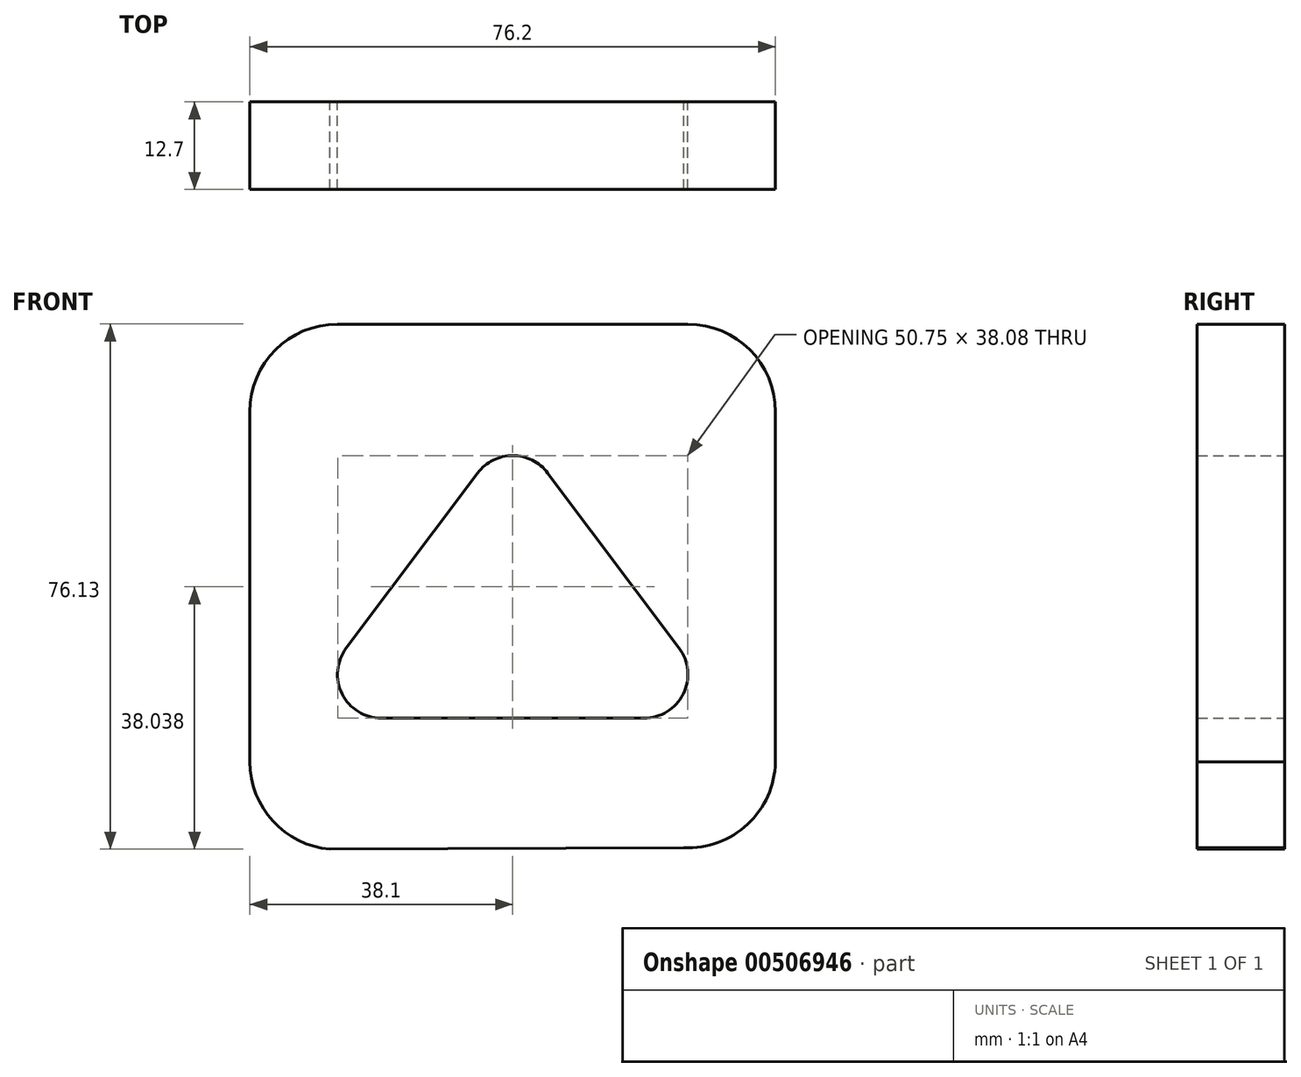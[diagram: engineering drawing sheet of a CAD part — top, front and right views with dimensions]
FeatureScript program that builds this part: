
annotation { "Feature Type Name" : "Feature", "Feature Type Description" : "" }
export const myFeature = defineFeature(function(context is Context, id is Id, definition is map)
    precondition{}
    {
        {
            var Q0;
            Q0=qCreatedBy(makeId("Front.planeOp"),FACE);
            var sketch = newSketch(context, id + "F0", { "sketchPlane" : qUnion([Q0])});
            skLineSegment(sketch, "E0", {"start": v(76.2, 12.68) * mm, "end": v(76.2, 63.48) * mm});
            skLineSegment(sketch, "E1", {"start": v(63.5, 76.18) * mm, "end": v(12.7, 76.18) * mm});
            skLineSegment(sketch, "E2", {"start": v(0, 63.48) * mm, "end": v(0, 12.7) * mm});
            skArc(sketch, "E3", {"start": v(13.97, 29.21) * mm, "mid": v(13.37, 22.56) * mm, "end": v(19.05, 19.05) * mm});
            skArc(sketch, "E4", {"start": v(57.15, 19.05) * mm, "mid": v(62.83, 22.56) * mm, "end": v(62.23, 29.21) * mm});
            skArc(sketch, "E5", {"start": v(43.18, 54.59) * mm, "mid": v(38.1, 57.13) * mm, "end": v(33.02, 54.59) * mm});
            skLineSegment(sketch, "E6", {"start": v(13.97, 29.21) * mm, "end": v(33.02, 54.59) * mm});
            skLineSegment(sketch, "E7", {"start": v(43.18, 54.59) * mm, "end": v(62.23, 29.21) * mm});
            skLineSegment(sketch, "E8", {"start": v(19.05, 19.05) * mm, "end": v(57.15, 19.05) * mm});
            skArc(sketch, "E9", {"start": v(12.7, 76.18) * mm, "mid": v(3.72, 72.46) * mm, "end": v(0, 63.48) * mm});
            skPoint(sketch, "E10.orphan", {"position": v(0, 76.18) * mm});
            skLineSegment(sketch, "E11", {"start": v(11.6, 0.05) * mm, "end": v(62.92, 0.26) * mm});
            skArc(sketch, "E12", {"start": v(0, 12.7) * mm, "mid": v(4.16, 3.3) * mm, "end": v(13.91, 0.06) * mm});
            skArc(sketch, "E13", {"start": v(76.2, 63.48) * mm, "mid": v(72.48, 72.46) * mm, "end": v(63.5, 76.18) * mm});
            skArc(sketch, "E14.trimOffspring", {"start": v(62.92, 0.26) * mm, "mid": v(72.18, 3.67) * mm, "end": v(76.2, 12.68) * mm});
            skSolve(sketch);
        }
        {
            var Q0;
            Q0=makeQuery(id+"F0.imprint","IMPRINT",FACE,{"disambiguationData":[TD([[makeQuery(id+"F0.imprint","IMPRINT",EDGE,{"derivedFrom":sQuery(id+"F0.wireOp",EDGE,"E0")}),1.0]])]});
            extrude(context, id + "F1", {"entities" : qUnion([Q0]), "depth" : 12.7 * mm});
        }
    });
